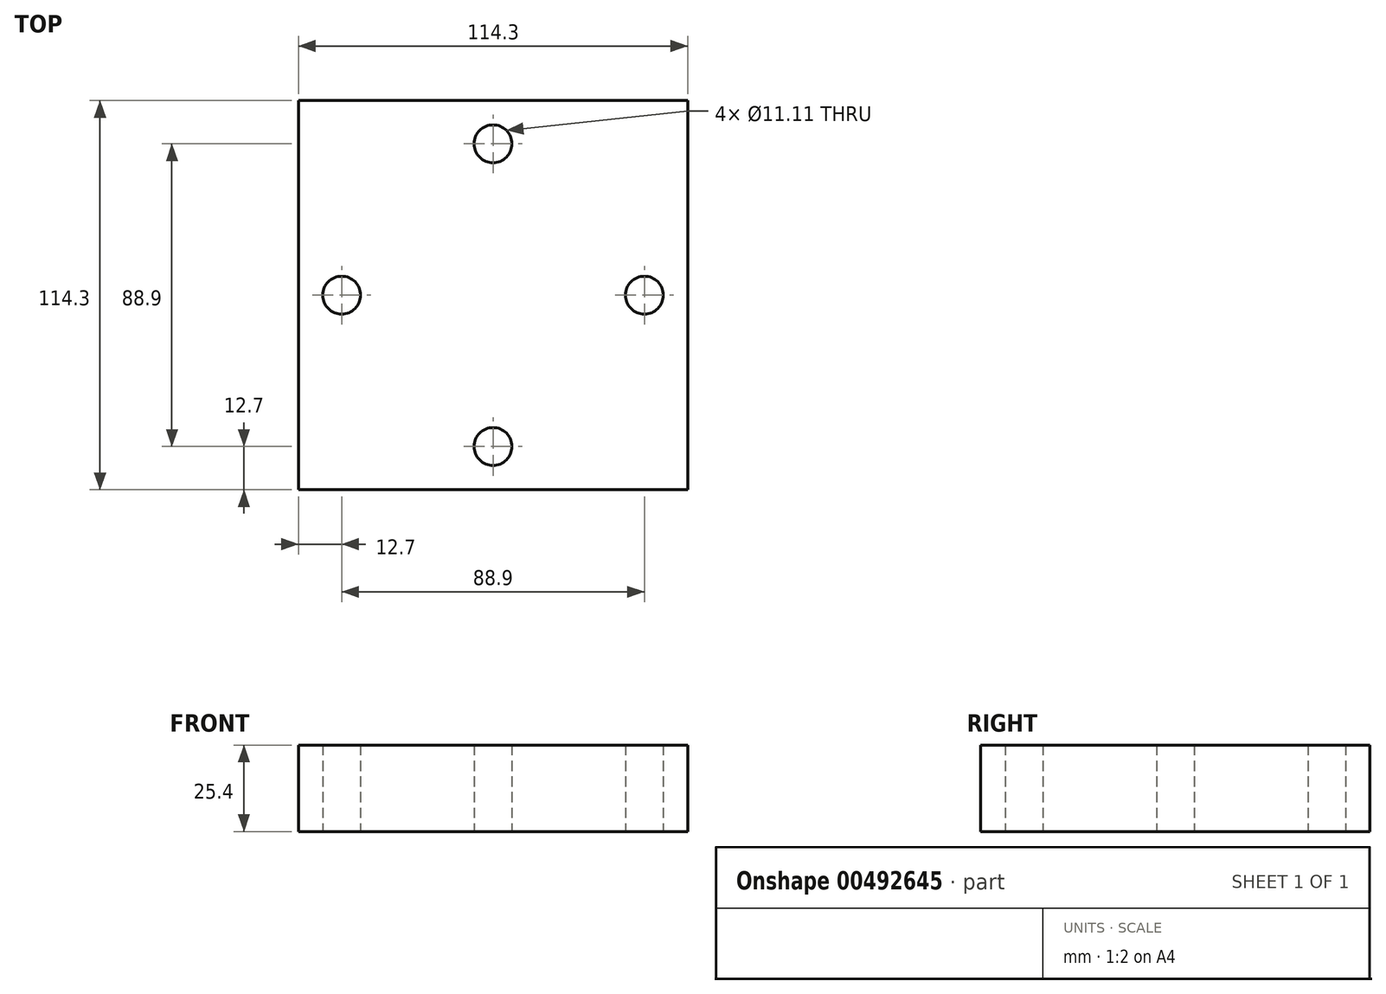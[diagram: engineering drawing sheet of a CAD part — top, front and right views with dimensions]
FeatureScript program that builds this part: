
annotation { "Feature Type Name" : "Feature", "Feature Type Description" : "" }
export const myFeature = defineFeature(function(context is Context, id is Id, definition is map)
    precondition{}
    {
        {
            var Q0;
            Q0=qCreatedBy(makeId("Top.planeOp"),FACE);
            var sketch = newSketch(context, id + "F0", { "sketchPlane" : qUnion([Q0])});
            skLineSegment(sketch, "E0.bottom", {"start": v(57.15, -57.15) * mm, "end": v(-57.15, -57.15) * mm});
            skLineSegment(sketch, "E0.top", {"start": v(57.15, 57.15) * mm, "end": v(-57.15, 57.15) * mm});
            skLineSegment(sketch, "E0.left", {"start": v(57.15, -57.15) * mm, "end": v(57.15, 57.15) * mm});
            skLineSegment(sketch, "E0.right", {"start": v(-57.15, -57.15) * mm, "end": v(-57.15, 57.15) * mm});
            skPoint(sketch, "E0.middle", {"position": v(0, 0) * mm});
            skCircle(sketch, "E1", {"center": v(0, 44.45) * mm, "radius": 5.56 * mm});
            skCircle(sketch, "E2", {"center": v(-44.45, 0) * mm, "radius": 5.56 * mm});
            skLineSegment(sketch, "E3", {"start": v(-57.15, 0) * mm, "end": v(57.15, 0) * mm, "construction": true});
            skLineSegment(sketch, "E4", {"start": v(0, 57.15) * mm, "end": v(0, -57.15) * mm, "construction": true});
            skCircle(sketch, "E5.MirrorC", {"center": v(0, -44.45) * mm, "radius": 5.56 * mm});
            skCircle(sketch, "E6.MirrorC", {"center": v(44.45, 0) * mm, "radius": 5.56 * mm});
            skSolve(sketch);
        }
        {
            var Q0;
            Q0 = qSketchRegion(id + "F0", true);
            extrude(context, id + "F1", {"entities" : qUnion([Q0]), "depth" : 25.4 * mm, "offsetDistance" : 25.4 * mm});
        }
    });
